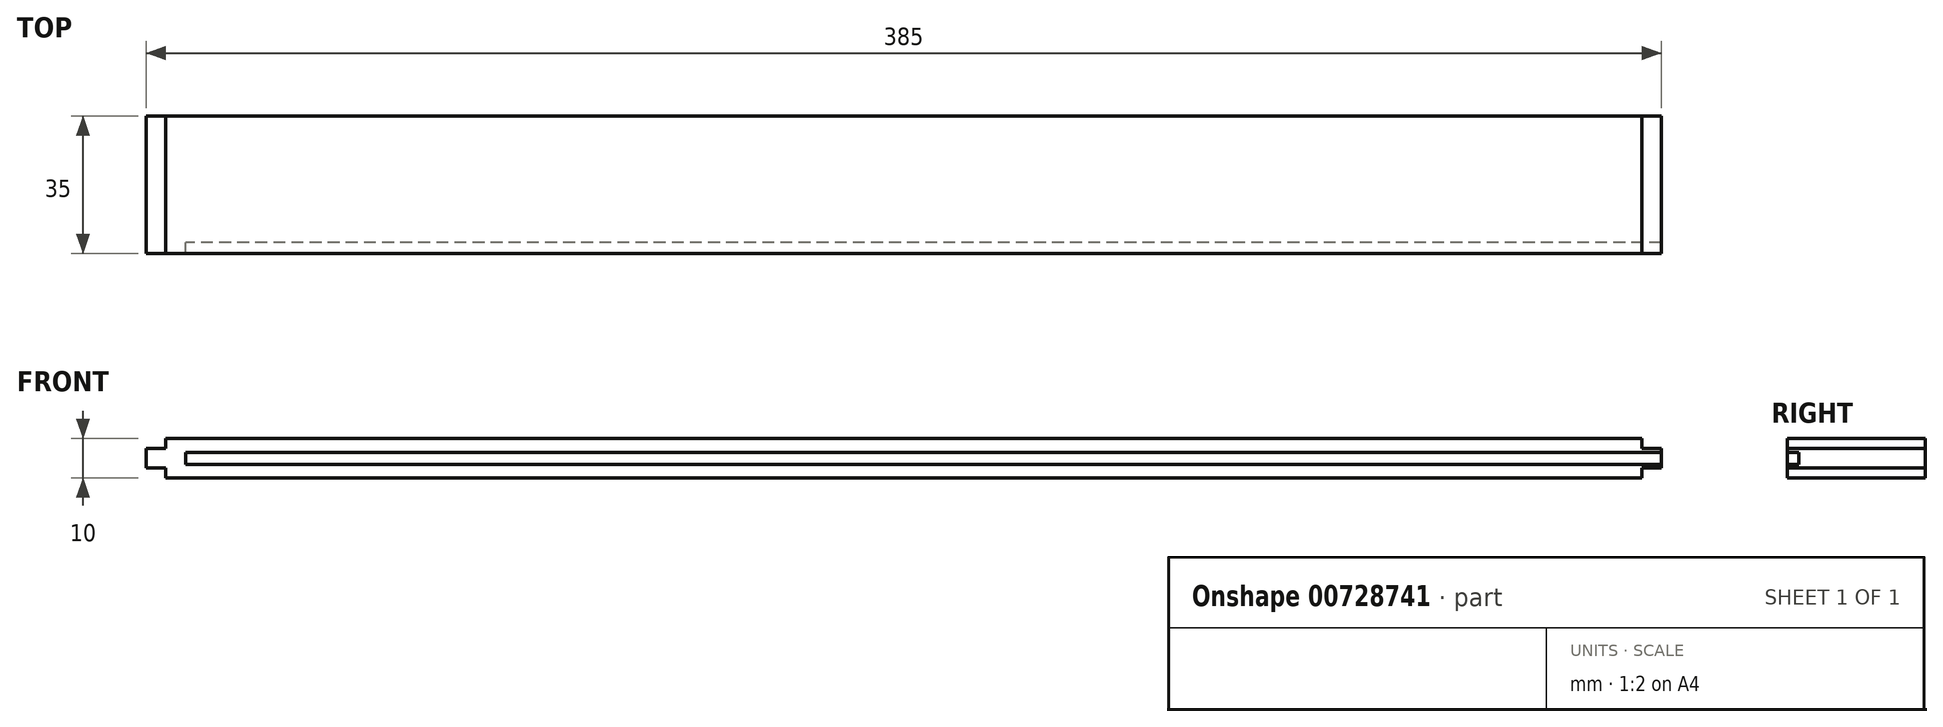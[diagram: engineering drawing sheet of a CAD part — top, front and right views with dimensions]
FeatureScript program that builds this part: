
annotation { "Feature Type Name" : "Feature", "Feature Type Description" : "" }
export const myFeature = defineFeature(function(context is Context, id is Id, definition is map)
    precondition{}
    {
        {
            var Q0;
            Q0=qCreatedBy(makeId("Front.planeOp"),FACE);
            var sketch = newSketch(context, id + "F0", { "sketchPlane" : qUnion([Q0])});
            skLineSegment(sketch, "E0", {"start": v(-226.93, 0) * mm, "end": v(-226.93, 2.5) * mm});
            skLineSegment(sketch, "E1", {"start": v(-226.93, 2.5) * mm, "end": v(-221.93, 2.5) * mm});
            skLineSegment(sketch, "E2", {"start": v(-221.93, 2.5) * mm, "end": v(-221.93, 5) * mm});
            skLineSegment(sketch, "E3", {"start": v(-221.93, 5) * mm, "end": v(153.07, 5) * mm});
            skLineSegment(sketch, "E4", {"start": v(153.07, -5) * mm, "end": v(-221.93, -5) * mm});
            skLineSegment(sketch, "E5", {"start": v(-221.93, -5) * mm, "end": v(-221.93, -2.5) * mm});
            skLineSegment(sketch, "E6", {"start": v(-221.93, -2.5) * mm, "end": v(-226.93, -2.5) * mm});
            skLineSegment(sketch, "E7", {"start": v(-226.93, -2.5) * mm, "end": v(-226.93, 0) * mm});
            skLineSegment(sketch, "E8", {"start": v(153.07, 2.5) * mm, "end": v(158.07, 2.5) * mm});
            skLineSegment(sketch, "E9", {"start": v(158.07, 2.5) * mm, "end": v(158.07, -2.5) * mm});
            skLineSegment(sketch, "E10", {"start": v(158.07, -2.5) * mm, "end": v(153.07, -2.5) * mm});
            skLineSegment(sketch, "E11", {"start": v(153.07, -2.5) * mm, "end": v(153.07, -5) * mm});
            skLineSegment(sketch, "E12", {"start": v(153.07, 5) * mm, "end": v(153.07, 2.5) * mm});
            skSolve(sketch);
        }
        {
            var Q0;
            Q0=makeQuery(id+"F0.imprint","IMPRINT",FACE,{"disambiguationData":[TD([[makeQuery(id+"F0.imprint","IMPRINT",EDGE,{"derivedFrom":sQuery(id+"F0.wireOp",EDGE,"E0")}),-1.0]])]});
            extrude(context, id + "F1", {"entities" : qUnion([Q0]), "depth" : 35 * mm, "offsetDistance" : 25 * mm});
        }
        {
            var Q0;
            Q0=qCreatedBy(makeId("Right.planeOp"),FACE);
            var sketch = newSketch(context, id + "F2", { "sketchPlane" : qUnion([Q0])});
            skLineSegment(sketch, "E13", {"start": v(-33.72, -2.54) * mm, "end": v(-30.72, -2.54) * mm});
            skLineSegment(sketch, "E14", {"start": v(-30.72, -2.54) * mm, "end": v(-30.72, 0.46) * mm});
            skLineSegment(sketch, "E15", {"start": v(-30.72, 0.46) * mm, "end": v(-33.72, 0.46) * mm});
            skLineSegment(sketch, "E16", {"start": v(-33.72, 0.46) * mm, "end": v(-33.72, -2.54) * mm});
            skSolve(sketch);
        }
        {
            var Q0;
            Q0=makeQuery(id+"F2.imprint","IMPRINT",FACE,{"disambiguationData":[TD([[makeQuery(id+"F2.imprint","IMPRINT",EDGE,{"derivedFrom":sQuery(id+"F2.wireOp",EDGE,"E13")}),1.0]])]});
            extrude(context, id + "F3", {"entities" : qUnion([Q0]), "depth" : 187.5 * mm, "offsetDistance" : 25 * mm, "hasSecondDirection" : true, "secondDirectionOppositeDirection" : true, "secondDirectionDepth" : 187.5 * mm});
        }
        {
            var Q0;
            Q0=makeQuery(id+"F1.opExtrude","SWEPT_BODY",BODY,{"disambiguationData":[OSD([sQuery(id+"F0.wireOp",EDGE,"E0"),sQuery(id+"F0.wireOp",EDGE,"E1"),sQuery(id+"F0.wireOp",EDGE,"E2"),sQuery(id+"F0.wireOp",EDGE,"E3"),sQuery(id+"F0.wireOp",EDGE,"E4"),sQuery(id+"F0.wireOp",EDGE,"E5"),sQuery(id+"F0.wireOp",EDGE,"E6"),sQuery(id+"F0.wireOp",EDGE,"E7"),sQuery(id+"F0.wireOp",EDGE,"E8"),sQuery(id+"F0.wireOp",EDGE,"E9"),sQuery(id+"F0.wireOp",EDGE,"E10"),sQuery(id+"F0.wireOp",EDGE,"E11"),sQuery(id+"F0.wireOp",EDGE,"E12")])]});
            transform(context, id + "F4", {"entities" : qUnion([Q0]), "transformType" : TransformType.TRANSLATION_3D, "dx" : 29.4 * mm, "dy" : 1.4 * mm, "dz" : -1 * mm, "makeCopy" : false});
        }
        {
            var Q0;
            Q0=makeQuery(id+"F3.opExtrude","SWEPT_BODY",BODY,{"disambiguationData":[OSD([sQuery(id+"F2.wireOp",EDGE,"E13"),sQuery(id+"F2.wireOp",EDGE,"E14"),sQuery(id+"F2.wireOp",EDGE,"E15"),sQuery(id+"F2.wireOp",EDGE,"E16")])]});
            var Q1;
            Q1=makeQuery(id+"F1.opExtrude","SWEPT_BODY",BODY,{"disambiguationData":[OSD([sQuery(id+"F0.wireOp",EDGE,"E0"),sQuery(id+"F0.wireOp",EDGE,"E1"),sQuery(id+"F0.wireOp",EDGE,"E2"),sQuery(id+"F0.wireOp",EDGE,"E3"),sQuery(id+"F0.wireOp",EDGE,"E4"),sQuery(id+"F0.wireOp",EDGE,"E5"),sQuery(id+"F0.wireOp",EDGE,"E6"),sQuery(id+"F0.wireOp",EDGE,"E7"),sQuery(id+"F0.wireOp",EDGE,"E8"),sQuery(id+"F0.wireOp",EDGE,"E9"),sQuery(id+"F0.wireOp",EDGE,"E10"),sQuery(id+"F0.wireOp",EDGE,"E11"),sQuery(id+"F0.wireOp",EDGE,"E12")])]});
            booleanBodies(context, id + "F5", {"operationType" : BooleanOperationType.SUBTRACTION, "tools" : qUnion([Q0]), "targets" : qUnion([Q1])});
        }
    });
